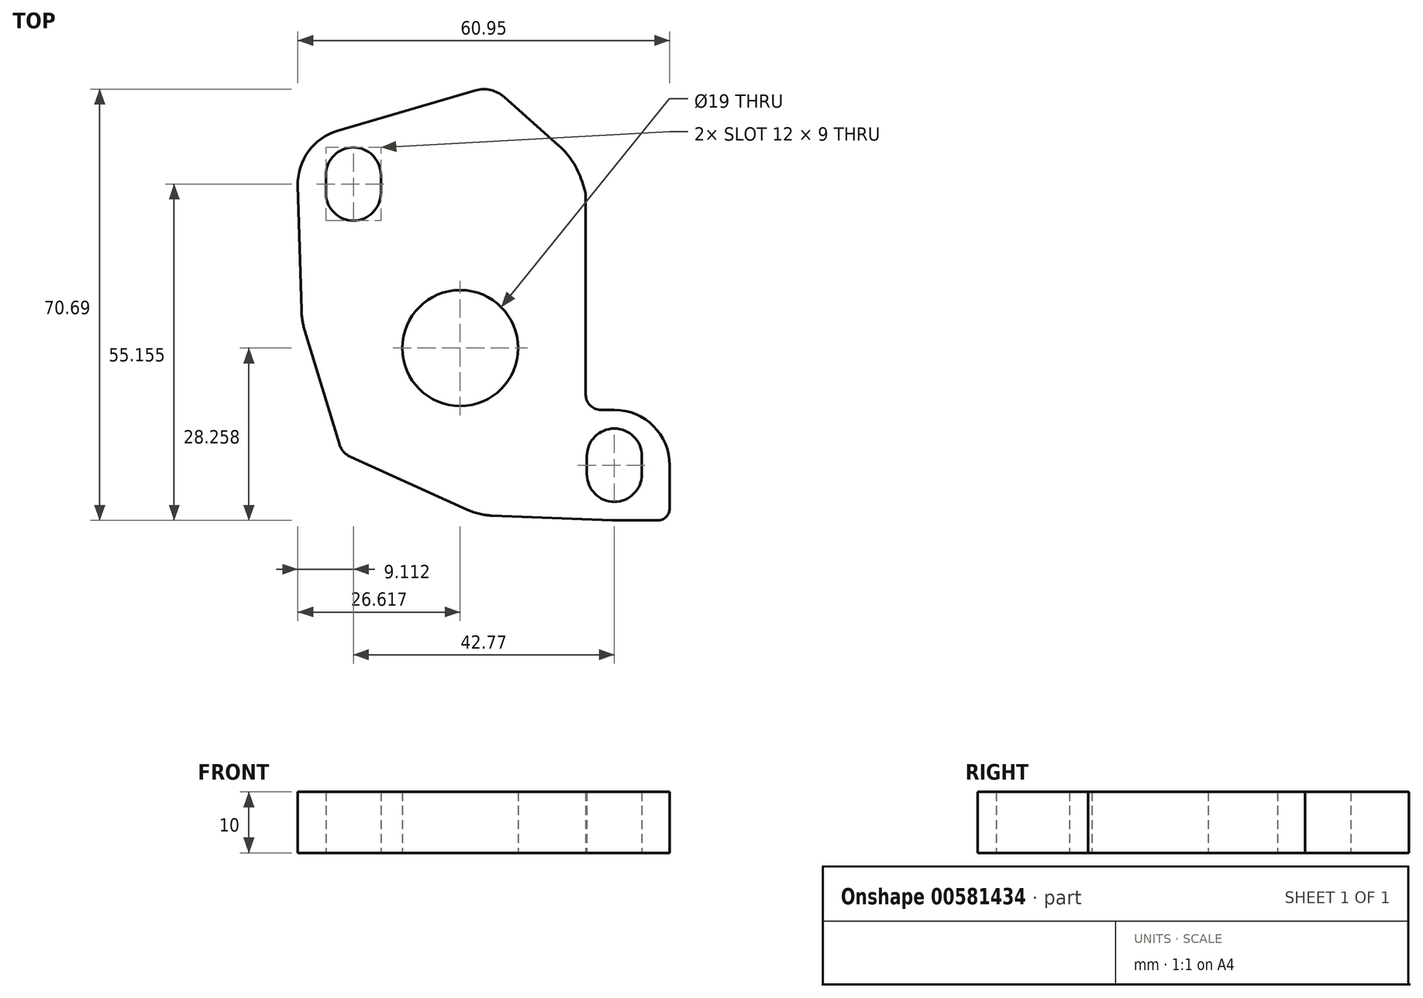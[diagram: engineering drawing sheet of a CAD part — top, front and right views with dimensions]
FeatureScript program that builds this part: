
annotation { "Feature Type Name" : "Feature", "Feature Type Description" : "" }
export const myFeature = defineFeature(function(context is Context, id is Id, definition is map)
    precondition{}
    {
        {
            var Q0;
            Q0=qCreatedBy(makeId("Top.planeOp"),FACE);
            var sketch = newSketch(context, id + "F0", { "sketchPlane" : qUnion([Q0])});
            skArc(sketch, "E0", {"start": v(-22.02, 29.45) * mm, "mid": v(-26.83, 26.06) * mm, "end": v(-28.57, 20.44) * mm});
            skPoint(sketch, "E0.first.point", {"position": v(-27.8, 17.04) * mm});
            skPoint(sketch, "E0.second.point", {"position": v(-25.68, 27.37) * mm});
            skPoint(sketch, "E0.third.point", {"position": v(-14.54, 28.36) * mm});
            skArc(sketch, "E1", {"start": v(5.24, 34.98) * mm, "mid": v(3.03, 36.12) * mm, "end": v(0.55, 36.04) * mm});
            skPoint(sketch, "E1.first.point", {"position": v(-2.66, 33.14) * mm});
            skPoint(sketch, "E1.second.point", {"position": v(2.23, 36.23) * mm});
            skPoint(sketch, "E1.third.point", {"position": v(6.64, 32.88) * mm});
            skArc(sketch, "E2", {"start": v(22.94, -34.45) * mm, "mid": v(23.12, -34.45) * mm, "end": v(23.3, -34.45) * mm});
            skPoint(sketch, "E2.first.point", {"position": v(17.86, -32.64) * mm});
            skPoint(sketch, "E2.second.point", {"position": v(29.98, -31.52) * mm});
            skPoint(sketch, "E2.third.point", {"position": v(25.66, -16.63) * mm});
            skArc(sketch, "E3", {"start": v(17.99, 21.16) * mm, "mid": v(16.49, 24.34) * mm, "end": v(14.2, 27) * mm});
            skPoint(sketch, "E3.first.point", {"position": v(9.2, 29.78) * mm});
            skPoint(sketch, "E3.second.point", {"position": v(14.99, 26.24) * mm});
            skPoint(sketch, "E3.third.point", {"position": v(17.9, 21.43) * mm});
            skArc(sketch, "E4", {"start": v(-21.76, -21.96) * mm, "mid": v(-21.08, -23.19) * mm, "end": v(-19.95, -24.03) * mm});
            skArc(sketch, "E5", {"start": v(-0.8, -32.7) * mm, "mid": v(1.17, -33.38) * mm, "end": v(3.24, -33.66) * mm});
            skArc(sketch, "E6", {"start": v(-27.99, 0.03) * mm, "mid": v(-27.83, -1.66) * mm, "end": v(-27.44, -3.3) * mm});
            skLineSegment(sketch, "E7", {"start": v(-22.02, 29.45) * mm, "end": v(0.55, 36.04) * mm});
            skLineSegment(sketch, "E8", {"start": v(-28.57, 20.44) * mm, "end": v(-27.99, 0.03) * mm});
            skLineSegment(sketch, "E9", {"start": v(-27.44, -3.3) * mm, "end": v(-21.76, -21.96) * mm});
            skPoint(sketch, "E9.endSnap0", {"position": v(-20.77, -23.5) * mm});
            skLineSegment(sketch, "E10", {"start": v(-19.95, -24.03) * mm, "end": v(-0.8, -32.7) * mm});
            skLineSegment(sketch, "E11", {"start": v(3.24, -33.66) * mm, "end": v(22.94, -34.45) * mm});
            skLineSegment(sketch, "E12", {"start": v(17.99, 21.16) * mm, "end": v(18.61, 19.21) * mm});
            skLineSegment(sketch, "E13", {"start": v(5.24, 34.98) * mm, "end": v(14.2, 27) * mm});
            skPoint(sketch, "E14.orphan", {"position": v(-21.3, -23.5) * mm});
            skArc(sketch, "E15", {"start": v(-14.97, 22.2) * mm, "mid": v(-19.47, 26.7) * mm, "end": v(-23.97, 22.2) * mm});
            skArc(sketch, "E16", {"start": v(-23.97, 19.2) * mm, "mid": v(-19.47, 14.7) * mm, "end": v(-14.97, 19.2) * mm});
            skLineSegment(sketch, "E17", {"start": v(-19.47, 22.2) * mm, "end": v(-19.47, 19.2) * mm, "construction": true});
            skLineSegment(sketch, "E18", {"start": v(-23.97, 22.2) * mm, "end": v(-23.97, 19.2) * mm});
            skLineSegment(sketch, "E19", {"start": v(-14.97, 19.2) * mm, "end": v(-14.97, 22.2) * mm});
            skArc(sketch, "E20", {"start": v(27.8, -23.89) * mm, "mid": v(23.3, -19.39) * mm, "end": v(18.8, -23.89) * mm});
            skArc(sketch, "E21", {"start": v(18.8, -26.89) * mm, "mid": v(23.3, -31.39) * mm, "end": v(27.8, -26.89) * mm});
            skLineSegment(sketch, "E22", {"start": v(23.3, -23.89) * mm, "end": v(23.3, -26.89) * mm, "construction": true});
            skLineSegment(sketch, "E23", {"start": v(18.8, -23.89) * mm, "end": v(18.8, -26.89) * mm});
            skLineSegment(sketch, "E24", {"start": v(27.8, -26.89) * mm, "end": v(27.8, -23.89) * mm});
            skArc(sketch, "E25", {"start": v(-17.17, 10.8) * mm, "mid": v(-13.1, 12.91) * mm, "end": v(-10.36, 16.57) * mm, "construction": true});
            skLineSegment(sketch, "E26", {"start": v(13.04, -20.86) * mm, "end": v(13.04, 3.17) * mm, "construction": true});
            skCircle(sketch, "E27", {"center": v(-1.96, -6.2) * mm, "radius": 9.5 * mm});
            skLineSegment(sketch, "E28", {"start": v(18.61, -13.82) * mm, "end": v(18.61, 19.21) * mm});
            skLineSegment(sketch, "E29", {"start": v(21.11, -16.32) * mm, "end": v(23.3, -16.32) * mm});
            skArc(sketch, "E30.filletArc", {"start": v(18.61, -13.82) * mm, "mid": v(19.34, -15.6) * mm, "end": v(21.11, -16.32) * mm});
            skPoint(sketch, "E31.trimOffspring.end.orphan", {"position": v(31.94, -22.64) * mm});
            skLineSegment(sketch, "E32", {"start": v(32.37, -25.39) * mm, "end": v(32.37, -32.45) * mm});
            skLineSegment(sketch, "E33", {"start": v(30.37, -34.45) * mm, "end": v(23.3, -34.45) * mm});
            skArc(sketch, "E34.trimOffspring", {"start": v(32.37, -25.39) * mm, "mid": v(29.71, -18.98) * mm, "end": v(23.3, -16.32) * mm});
            skPoint(sketch, "E35.visualSharp", {"position": v(32.37, -34.45) * mm});
            skArc(sketch, "E35.filletArc", {"start": v(30.37, -34.45) * mm, "mid": v(31.78, -33.87) * mm, "end": v(32.37, -32.45) * mm});
            skPoint(sketch, "E36.orphan", {"position": v(0, -33.07) * mm});
            skLineSegment(sketch, "E37", {"start": v(-19.47, 19.2) * mm, "end": v(-1.96, -6.2) * mm, "construction": true});
            skLineSegment(sketch, "E38", {"start": v(-1.96, -6.2) * mm, "end": v(23.3, -23.89) * mm, "construction": true});
            skSolve(sketch);
        }
        {
            var Q0;
            Q0=makeQuery(id+"F0.imprint","IMPRINT",FACE,{"disambiguationData":[TD([[makeQuery(id+"F0.imprint","IMPRINT",EDGE,{"derivedFrom":sQuery(id+"F0.wireOp",EDGE,"E0")}),1.0]])]});
            extrude(context, id + "F1", {"entities" : qUnion([Q0]), "depth" : 10 * mm, "offsetDistance" : 25 * mm});
        }
    });
